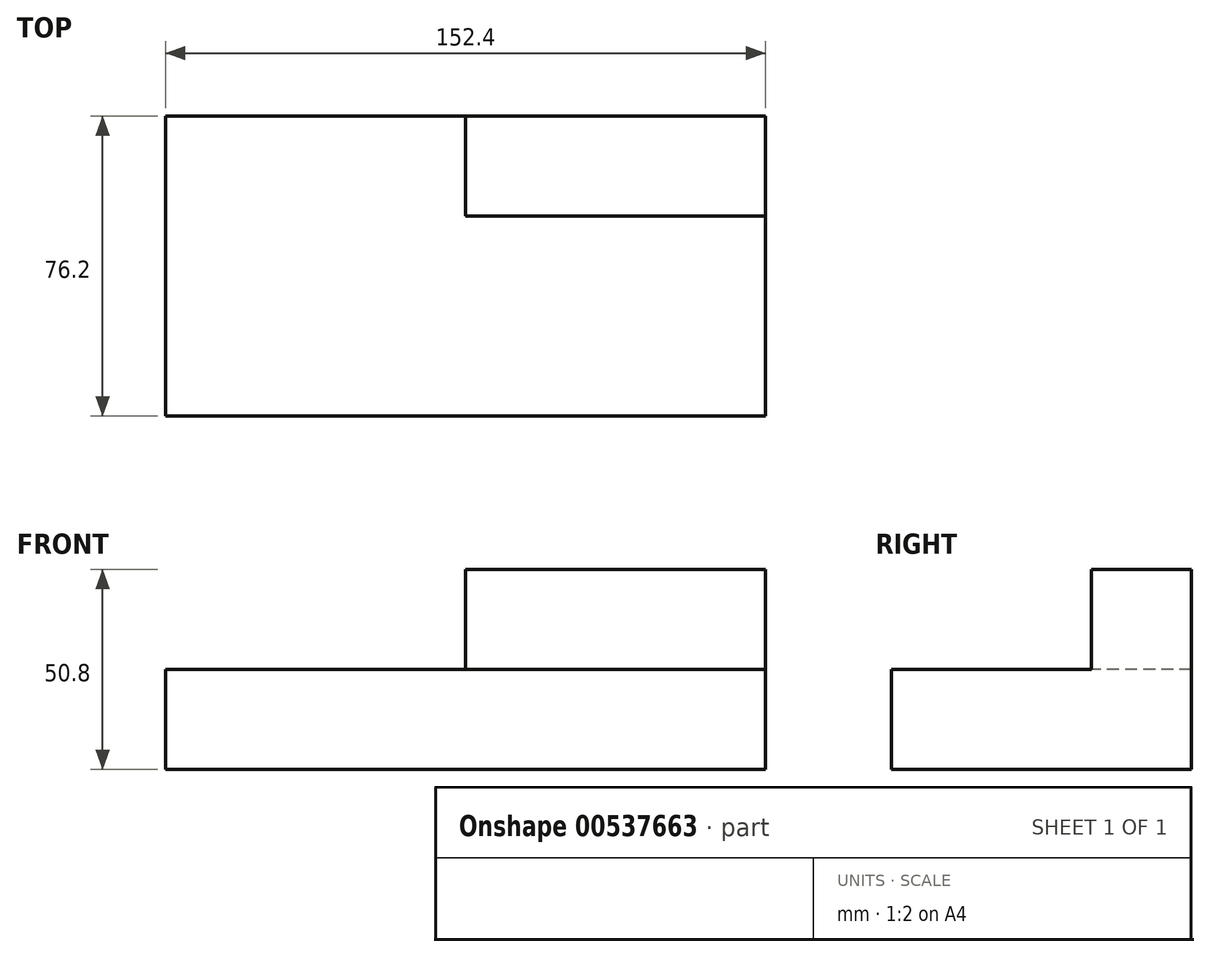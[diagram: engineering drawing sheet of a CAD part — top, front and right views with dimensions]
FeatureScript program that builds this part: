
annotation { "Feature Type Name" : "Feature", "Feature Type Description" : "" }
export const myFeature = defineFeature(function(context is Context, id is Id, definition is map)
    precondition{}
    {
        {
            var Q0;
            Q0=qCreatedBy(makeId("Top.planeOp"),FACE);
            var sketch = newSketch(context, id + "F0", { "sketchPlane" : qUnion([Q0])});
            skLineSegment(sketch, "E0.bottom", {"start": v(-68.95, 33.3) * mm, "end": v(83.45, 33.3) * mm});
            skLineSegment(sketch, "E0.top", {"start": v(-68.95, -42.9) * mm, "end": v(83.45, -42.9) * mm});
            skLineSegment(sketch, "E0.left", {"start": v(-68.95, 33.3) * mm, "end": v(-68.95, -42.9) * mm});
            skLineSegment(sketch, "E0.right", {"start": v(83.45, 33.3) * mm, "end": v(83.45, -42.9) * mm});
            skLineSegment(sketch, "E1.bottom", {"start": v(83.45, 33.3) * mm, "end": v(7.25, 33.3) * mm});
            skLineSegment(sketch, "E1.top", {"start": v(83.45, 7.9) * mm, "end": v(7.25, 7.9) * mm});
            skLineSegment(sketch, "E1.left", {"start": v(83.45, 33.3) * mm, "end": v(83.45, 7.9) * mm});
            skLineSegment(sketch, "E1.right", {"start": v(7.25, 33.3) * mm, "end": v(7.25, 7.9) * mm});
            skLineSegment(sketch, "E2.bottom", {"start": v(83.45, -17.5) * mm, "end": v(7.25, -17.5) * mm});
            skLineSegment(sketch, "E2.top", {"start": v(83.45, -42.9) * mm, "end": v(7.25, -42.9) * mm});
            skLineSegment(sketch, "E2.left", {"start": v(83.45, -17.5) * mm, "end": v(83.45, -42.9) * mm});
            skLineSegment(sketch, "E2.right", {"start": v(7.25, -17.5) * mm, "end": v(7.25, -42.9) * mm});
            skSolve(sketch);
        }
        {
            var Q0;
            Q0=makeQuery(id+"F0.imprint","IMPRINT",FACE,{"disambiguationData":[TD([[makeQuery(id+"F0.imprint","IMPRINT",EDGE,{"derivedFrom":sQuery(id+"F0.wireOp",EDGE,"E0.bottom")}),-1.0]])]});
            extrude(context, id + "F1", {"entities" : qUnion([Q0]), "depth" : 50.8 * mm, "offsetDistance" : 25.4 * mm});
        }
        {
            var Q0;
            Q0 = qSketchRegion(id + "F0", true);
            extrude(context, id + "F2", {"entities" : qUnion([Q0]), "operationType" : NewBodyOperationType.ADD, "depth" : 25.4 * mm, "offsetDistance" : 25.4 * mm});
        }
    });
